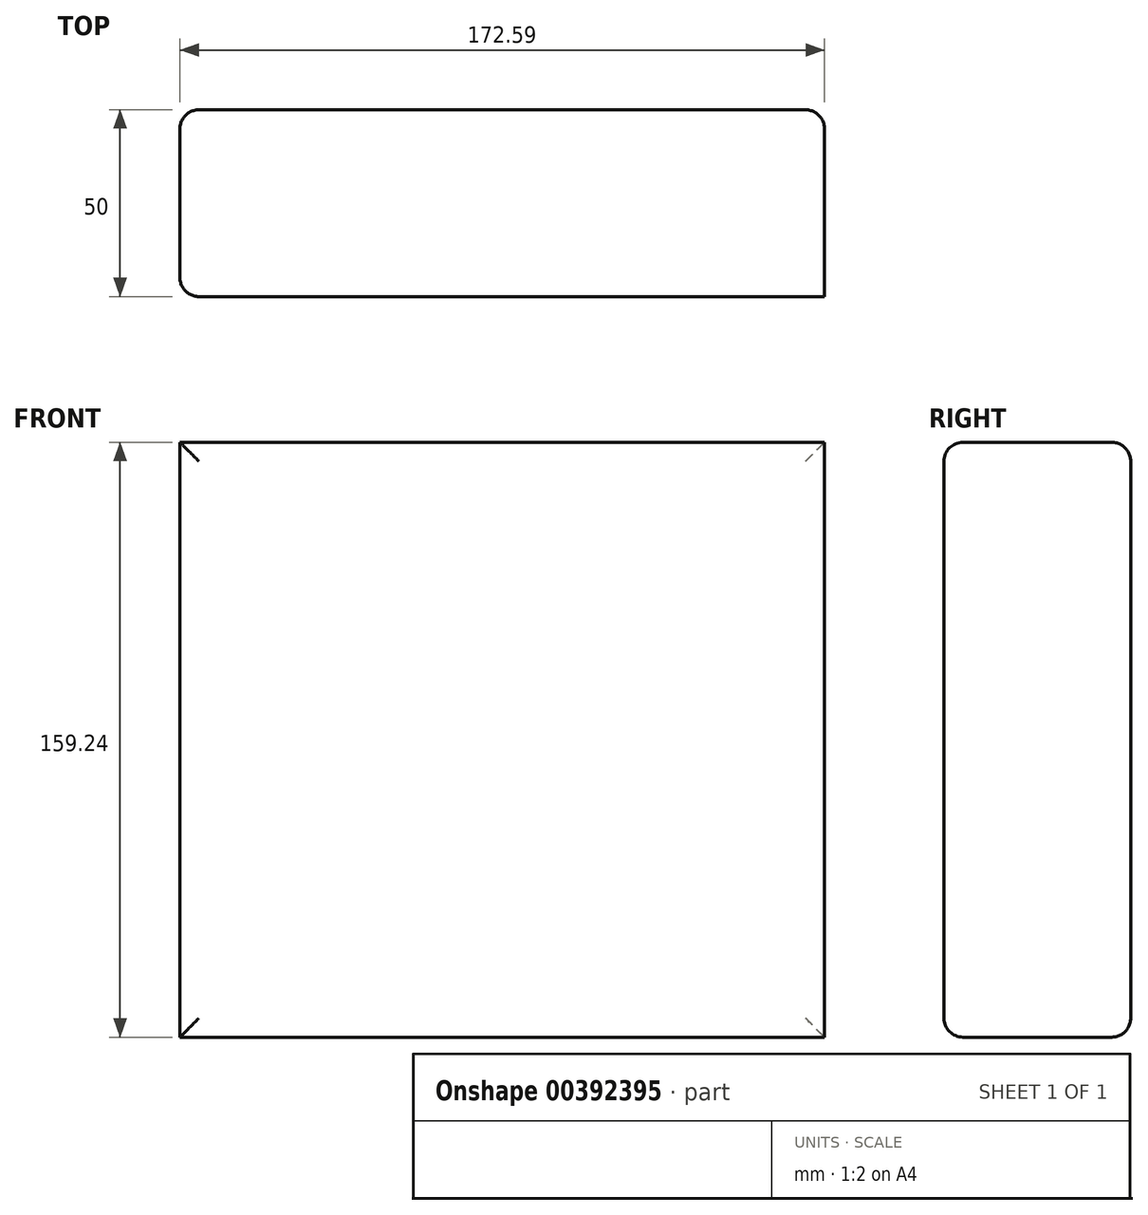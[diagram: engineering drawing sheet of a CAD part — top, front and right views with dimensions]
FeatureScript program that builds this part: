
annotation { "Feature Type Name" : "Feature", "Feature Type Description" : "" }
export const myFeature = defineFeature(function(context is Context, id is Id, definition is map)
    precondition{}
    {
        {
            var Q0;
            Q0=qCreatedBy(makeId("Front.planeOp"),FACE);
            var sketch = newSketch(context, id + "F0", { "sketchPlane" : qUnion([Q0])});
            skLineSegment(sketch, "E0.bottom", {"start": v(0, -27.03) * mm, "end": v(0, -27.03) * mm});
            skLineSegment(sketch, "E0.top", {"start": v(0, 27.03) * mm, "end": v(0, 27.03) * mm});
            skLineSegment(sketch, "E0.left", {"start": v(0, -27.03) * mm, "end": v(0, 27.03) * mm});
            skLineSegment(sketch, "E0.right", {"start": v(0, -27.03) * mm, "end": v(0, 27.03) * mm});
            skPoint(sketch, "E0.middle", {"position": v(0, 0) * mm});
            skLineSegment(sketch, "E1.bottom", {"start": v(85.32, 79.34) * mm, "end": v(-87.27, 79.34) * mm});
            skLineSegment(sketch, "E1.top", {"start": v(85.32, -79.9) * mm, "end": v(-87.27, -79.9) * mm});
            skLineSegment(sketch, "E1.left", {"start": v(85.32, 79.34) * mm, "end": v(85.32, -79.9) * mm});
            skLineSegment(sketch, "E1.right", {"start": v(-87.27, 79.34) * mm, "end": v(-87.27, -79.9) * mm});
            skPoint(sketch, "E1.middle", {"position": v(-0.98, -0.28) * mm});
            skSolve(sketch);
        }
        {
            var Q0;
            Q0 = qSketchRegion(id + "F0", true);
            extrude(context, id + "F1", {"entities" : qUnion([Q0]), "depth" : 50 * mm});
        }
        {
            var Q0;
            Q0=makeQuery(id+"F1.opExtrude","CAP_EDGE",EDGE,{"disambiguationData":[OSD([sQuery(id+"F0.wireOp",EDGE,"E1.bottom")])],"isStart":false});
            var Q1;
            Q1=makeQuery(id+"F1.opExtrude","CAP_EDGE",EDGE,{"disambiguationData":[OSD([sQuery(id+"F0.wireOp",EDGE,"E1.right")])],"isStart":false});
            var Q2;
            Q2=makeQuery(id+"F1.opExtrude","CAP_EDGE",EDGE,{"disambiguationData":[OSD([sQuery(id+"F0.wireOp",EDGE,"E1.bottom")])],"isStart":true});
            var Q3;
            Q3=makeQuery(id+"F1.opExtrude","CAP_FACE",FACE,{"disambiguationData":[OSD([sQuery(id+"F0.wireOp",EDGE,"E1.bottom"),sQuery(id+"F0.wireOp",EDGE,"E1.top"),sQuery(id+"F0.wireOp",EDGE,"E1.left"),sQuery(id+"F0.wireOp",EDGE,"E1.right")])],"isStart":true});
            var Q4;
            Q4=makeQuery(id+"F1.opExtrude","CAP_EDGE",EDGE,{"disambiguationData":[OSD([sQuery(id+"F0.wireOp",EDGE,"E1.top")])],"isStart":false});
            fillet(context, id + "F2", {"entities" : qUnion([Q0, Q1, Q2, Q3, Q4]), "radius" : 5.08 * mm, "tangentPropagation" : true, "allowEdgeOverflow" : false});
        }
    });
